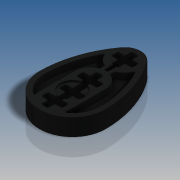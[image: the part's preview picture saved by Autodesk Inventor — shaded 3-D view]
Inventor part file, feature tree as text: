
AUTODESK INVENTOR PART (.ipt)
format: ipt  version: 2016 SP2 (Build 200236200, 236)  size: 420,352 bytes
history: native  units: in
note: dims shown in document units (in); Inventor stores cm internally (conversion verified against a paired STEP export)
features: extrude x3, sketch x2, fillet x1
ambient origin geometry x8: Origin, YZ Plane, XZ Plane, XY Plane, X Axis, Y Axis, Z Axis, Center Point
bodies: Solid1 (feature_tree)
feature tree (6):
  sketch  "Sketch2"  dims[d0=0.5984in d1=0.4724in]
  extrude  "Extrusion1"  Depth=0.4724in
  extrude  "Extrusion2"  Depth=0.0079in
  extrude  "Extrusion3"  Depth=0.0079in
  fillet  "Fillet1"  Radius=0.1575in
  sketch  "Sketch3"  dims[d2=0.2835in d3=0.9449in d4=0.189in d5=0.1575in d6=0.1575in d7=0.063in d8=0.0472in d9=0.0315in d10=0.0945in d11=0.1575in d13=0.0315in d14=0.0in d15=0.1575in d16=0.0in d17=0.2205in d18=0.0157in d19=0.0in d20=0.0039in d21=0.0079in]
